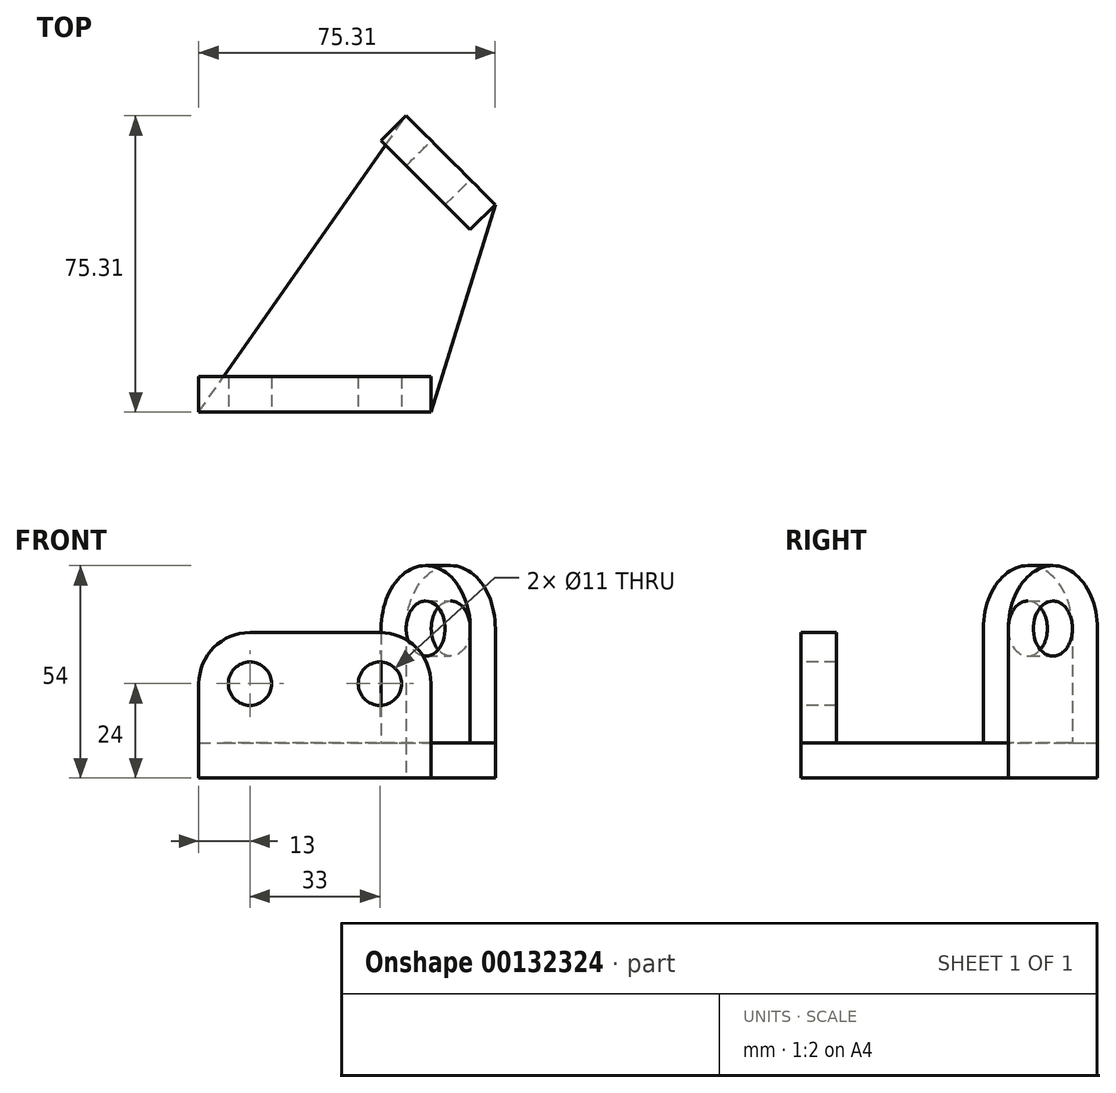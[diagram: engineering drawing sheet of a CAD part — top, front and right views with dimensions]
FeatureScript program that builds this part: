
annotation { "Feature Type Name" : "Feature", "Feature Type Description" : "" }
export const myFeature = defineFeature(function(context is Context, id is Id, definition is map)
    precondition{}
    {
        {
            var Q0;
            Q0=qCreatedBy(makeId("Top.planeOp"),FACE);
            var sketch = newSketch(context, id + "F0", { "sketchPlane" : qUnion([Q0])});
            skLineSegment(sketch, "E0", {"start": v(0, 0) * mm, "end": v(52.69, 75.31) * mm});
            skLineSegment(sketch, "E1", {"start": v(52.69, 75.31) * mm, "end": v(75.31, 52.69) * mm});
            skLineSegment(sketch, "E2", {"start": v(75.31, 52.69) * mm, "end": v(59, 0) * mm});
            skLineSegment(sketch, "E3", {"start": v(59, 0) * mm, "end": v(0, 0) * mm});
            skLineSegment(sketch, "E4", {"start": v(52.69, 75.31) * mm, "end": v(75.31, 75.31) * mm, "construction": true});
            skLineSegment(sketch, "E5", {"start": v(64, 64) * mm, "end": v(0, 0) * mm, "construction": true});
            skSolve(sketch);
        }
        {
            var Q0;
            Q0=makeQuery(id+"F0.imprint","IMPRINT",FACE,{"disambiguationData":[TD([[makeQuery(id+"F0.imprint","IMPRINT",EDGE,{"derivedFrom":sQuery(id+"F0.wireOp",EDGE,"E0")}),-1.0]])]});
            extrude(context, id + "F1", {"entities" : qUnion([Q0]), "depth" : 9 * mm});
        }
        {
            var Q0;
            Q0=makeQuery(id+"F1.opExtrude","SWEPT_FACE",FACE,{"disambiguationData":[OSD([sQuery(id+"F0.wireOp",EDGE,"E1")])]});
            var sketch = newSketch(context, id + "F2", { "sketchPlane" : qUnion([Q0])});
            skLineSegment(sketch, "E6", {"start": v(-16, 9) * mm, "end": v(-16, 38) * mm});
            skLineSegment(sketch, "E7", {"start": v(16, 38) * mm, "end": v(16, 9) * mm});
            skArc(sketch, "E8", {"start": v(16, 38) * mm, "mid": v(0, 54) * mm, "end": v(-16, 38) * mm});
            skCircle(sketch, "E9", {"center": v(0, 38) * mm, "radius": 7 * mm});
            skSolve(sketch);
        }
        {
            var Q0;
            Q0=makeQuery(id+"F2.imprint","IMPRINT",FACE,{"disambiguationData":[TD([[makeQuery(id+"F2.imprint","IMPRINT",EDGE,{"derivedFrom":sQuery(id+"F2.wireOp",EDGE,"E6")}),-1.0]])]});
            extrude(context, id + "F3", {"entities" : qUnion([Q0]), "operationType" : NewBodyOperationType.ADD, "oppositeDirection" : true, "depth" : 9 * mm});
        }
        {
            var Q0;
            Q0=makeQuery(id+"F1.opExtrude","SWEPT_FACE",FACE,{"disambiguationData":[OSD([sQuery(id+"F0.wireOp",EDGE,"E3")])]});
            var sketch = newSketch(context, id + "F4", { "sketchPlane" : qUnion([Q0])});
            skLineSegment(sketch, "E10", {"start": v(0, 9) * mm, "end": v(59, 9) * mm});
            skLineSegment(sketch, "E11", {"start": v(59, 9) * mm, "end": v(59, 24) * mm});
            skLineSegment(sketch, "E12", {"start": v(0, 24) * mm, "end": v(0, 9) * mm});
            skLineSegment(sketch, "E13", {"start": v(13, 37) * mm, "end": v(46, 37) * mm});
            skArc(sketch, "E14", {"start": v(0, 24) * mm, "mid": v(3.8, 33.2) * mm, "end": v(13, 37) * mm});
            skArc(sketch, "E15", {"start": v(59, 24) * mm, "mid": v(55.2, 33.2) * mm, "end": v(46, 37) * mm});
            skCircle(sketch, "E16", {"center": v(13, 24) * mm, "radius": 5.5 * mm});
            skCircle(sketch, "E17", {"center": v(46, 24) * mm, "radius": 5.5 * mm});
            skSolve(sketch);
        }
        {
            var Q0;
            Q0=makeQuery(id+"F4.imprint","IMPRINT",FACE,{"disambiguationData":[TD([[makeQuery(id+"F4.imprint","IMPRINT",EDGE,{"derivedFrom":sQuery(id+"F4.wireOp",EDGE,"E10")}),-1.0]])]});
            extrude(context, id + "F5", {"entities" : qUnion([Q0]), "operationType" : NewBodyOperationType.ADD, "oppositeDirection" : true, "depth" : 9 * mm});
        }
    });
